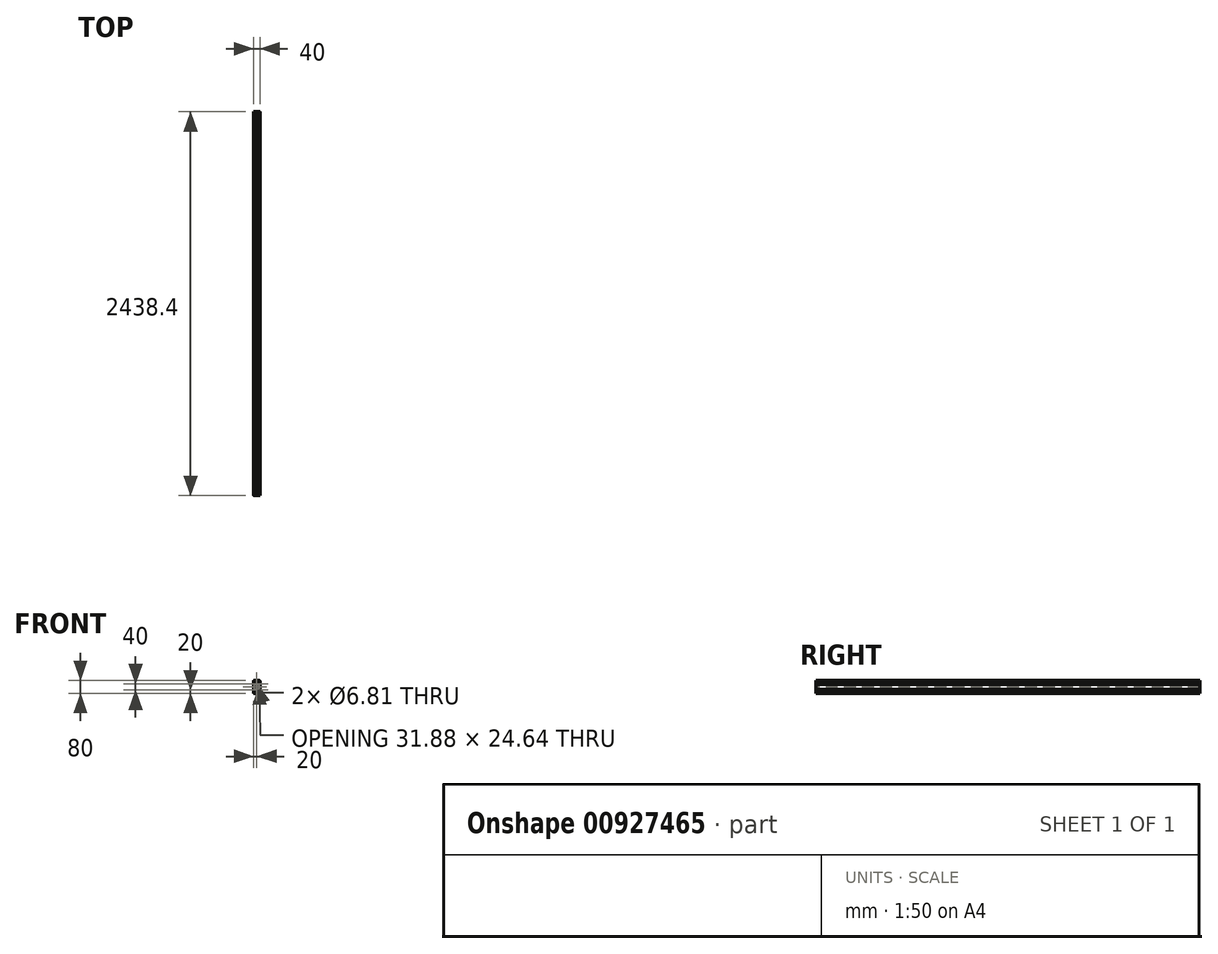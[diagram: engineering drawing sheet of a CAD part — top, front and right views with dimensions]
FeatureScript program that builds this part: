
annotation { "Feature Type Name" : "Feature", "Feature Type Description" : "" }
export const myFeature = defineFeature(function(context is Context, id is Id, definition is map)
    precondition{}
    {
        {
            var Q0;
            Q0=qCreatedBy(makeId("Front.planeOp"),FACE);
            var sketch = newSketch(context, id + "F0", { "sketchPlane" : qUnion([Q0])});
            skLineSegment(sketch, "E0.top", {"start": v(18.35, 40) * mm, "end": v(4.06, 40) * mm});
            skPoint(sketch, "E0.middle", {"position": v(0, 0) * mm});
            skArc(sketch, "E1", {"start": v(0, 16.6) * mm, "mid": v(3.4, 20) * mm, "end": v(0, 23.4) * mm});
            skLineSegment(sketch, "E2.bottom", {"start": v(20, 24.07) * mm, "end": v(15.94, 24.07) * mm});
            skLineSegment(sketch, "E2.top", {"start": v(20, 15.94) * mm, "end": v(15.94, 15.94) * mm});
            skLineSegment(sketch, "E3.top", {"start": v(15.94, 9.72) * mm, "end": v(12.62, 9.72) * mm});
            skLineSegment(sketch, "E4.right", {"start": v(15.94, 30.29) * mm, "end": v(15.94, 24.07) * mm});
            skLineSegment(sketch, "E5.MirrorCS", {"start": v(4.06, 40) * mm, "end": v(4.06, 35.94) * mm});
            skLineSegment(sketch, "E6.MirrorCS", {"start": v(10.28, 35.94) * mm, "end": v(4.06, 35.94) * mm});
            skLineSegment(sketch, "E7.MirrorCS", {"start": v(10.28, 35.94) * mm, "end": v(10.28, 32.62) * mm});
            skLineSegment(sketch, "E8.trimOffspring", {"start": v(20, 24.07) * mm, "end": v(20, 38.35) * mm});
            skLineSegment(sketch, "E9.trimOffspring", {"start": v(15.94, 15.94) * mm, "end": v(15.94, 9.72) * mm});
            skLineSegment(sketch, "E10.bottom", {"start": v(15.94, 30.29) * mm, "end": v(12.62, 30.29) * mm});
            skLineSegment(sketch, "E11.trimOffspring", {"start": v(7.68, 25.35) * mm, "end": v(7.68, 14.65) * mm});
            skLineSegment(sketch, "E12.trimOffspring", {"start": v(5.35, 27.68) * mm, "end": v(-5.35, 27.68) * mm});
            skLineSegment(sketch, "E13.trimOffspring", {"start": v(10.28, 32.62) * mm, "end": v(5.35, 27.68) * mm});
            skLineSegment(sketch, "E14.trimOffspring", {"start": v(12.62, 30.29) * mm, "end": v(7.68, 25.35) * mm});
            skLineSegment(sketch, "E15.trimOffspring", {"start": v(5.35, 12.32) * mm, "end": v(-5.35, 12.32) * mm});
            skLineSegment(sketch, "E16", {"start": v(11.25, 6.41) * mm, "end": v(15.94, 6.41) * mm});
            skLineSegment(sketch, "E17.trimOffspring", {"start": v(11.25, 6.41) * mm, "end": v(5.35, 12.32) * mm});
            skLineSegment(sketch, "E18.trimOffspring", {"start": v(12.62, 9.72) * mm, "end": v(7.68, 14.65) * mm});
            skPoint(sketch, "E19.visualSharp", {"position": v(20, 40) * mm});
            skArc(sketch, "E19.filletArc", {"start": v(20, 38.35) * mm, "mid": v(19.52, 39.52) * mm, "end": v(18.35, 40) * mm});
            skLineSegment(sketch, "E20.MirrorCS", {"start": v(15.94, -9.71) * mm, "end": v(12.62, -9.71) * mm});
            skLineSegment(sketch, "E21.MirrorCS", {"start": v(10.28, -35.94) * mm, "end": v(10.28, -32.62) * mm});
            skLineSegment(sketch, "E22.MirrorCS", {"start": v(15.94, -9.72) * mm, "end": v(12.62, -9.72) * mm});
            skArc(sketch, "E23.MirrorCS", {"start": v(20, -38.35) * mm, "mid": v(19.52, -39.52) * mm, "end": v(18.35, -40) * mm});
            skLineSegment(sketch, "E24.MirrorCS", {"start": v(15.94, -30.29) * mm, "end": v(12.62, -30.29) * mm});
            skLineSegment(sketch, "E25.MirrorCS", {"start": v(20, -24.07) * mm, "end": v(15.94, -24.07) * mm});
            skLineSegment(sketch, "E26.MirrorCS", {"start": v(5.35, -27.68) * mm, "end": v(-5.35, -27.68) * mm});
            skArc(sketch, "E27.MirrorCS", {"start": v(0, -16.6) * mm, "mid": v(3.4, -20) * mm, "end": v(0, -23.4) * mm});
            skLineSegment(sketch, "E28.MirrorCS", {"start": v(5.35, -12.32) * mm, "end": v(-5.35, -12.32) * mm});
            skLineSegment(sketch, "E29.MirrorCS", {"start": v(7.68, -25.35) * mm, "end": v(7.68, -14.65) * mm});
            skLineSegment(sketch, "E30.MirrorCS", {"start": v(10.28, -35.94) * mm, "end": v(4.06, -35.94) * mm});
            skLineSegment(sketch, "E31.MirrorCS", {"start": v(15.94, -30.28) * mm, "end": v(15.94, -24.07) * mm});
            skLineSegment(sketch, "E32.MirrorCS", {"start": v(20, -24.07) * mm, "end": v(20, -38.35) * mm});
            skLineSegment(sketch, "E33.MirrorCS", {"start": v(20, -24.06) * mm, "end": v(15.94, -24.06) * mm});
            skLineSegment(sketch, "E34.MirrorCS", {"start": v(20, -15.93) * mm, "end": v(15.94, -15.93) * mm});
            skLineSegment(sketch, "E35.MirrorCS", {"start": v(18.35, -40) * mm, "end": v(4.06, -40) * mm});
            skLineSegment(sketch, "E36.MirrorCS", {"start": v(4.06, -40) * mm, "end": v(4.06, -35.94) * mm});
            skLineSegment(sketch, "E37.MirrorCS", {"start": v(11.25, -6.41) * mm, "end": v(15.94, -6.41) * mm});
            skLineSegment(sketch, "E38.MirrorCS", {"start": v(15.94, -15.93) * mm, "end": v(15.94, -9.72) * mm});
            skPoint(sketch, "E39.MirrorP", {"position": v(20, -40) * mm});
            skLineSegment(sketch, "E40.MirrorCS", {"start": v(12.62, -30.29) * mm, "end": v(7.68, -25.35) * mm});
            skLineSegment(sketch, "E41.MirrorCS", {"start": v(11.25, -6.41) * mm, "end": v(5.35, -12.32) * mm});
            skLineSegment(sketch, "E42.MirrorCS", {"start": v(12.62, -9.72) * mm, "end": v(7.68, -14.65) * mm});
            skLineSegment(sketch, "E43.MirrorCS", {"start": v(10.28, -32.62) * mm, "end": v(5.35, -27.68) * mm});
            skLineSegment(sketch, "E44", {"start": v(15.94, 6.41) * mm, "end": v(15.94, -6.41) * mm});
            skLineSegment(sketch, "E45", {"start": v(20, 15.94) * mm, "end": v(20, -15.93) * mm});
            skLineSegment(sketch, "E46.MirrorCS", {"start": v(-15.94, -9.71) * mm, "end": v(-12.62, -9.71) * mm});
            skLineSegment(sketch, "E47.MirrorCS", {"start": v(-20, 24.07) * mm, "end": v(-15.94, 24.07) * mm});
            skLineSegment(sketch, "E48.MirrorCS", {"start": v(-15.94, 9.72) * mm, "end": v(-12.62, 9.72) * mm});
            skLineSegment(sketch, "E49.MirrorCS", {"start": v(-10.28, 35.94) * mm, "end": v(-10.28, 32.62) * mm});
            skLineSegment(sketch, "E50.MirrorCS", {"start": v(-10.28, -35.94) * mm, "end": v(-10.28, -32.62) * mm});
            skLineSegment(sketch, "E51.MirrorCS", {"start": v(-20, -24.06) * mm, "end": v(-15.94, -24.06) * mm});
            skLineSegment(sketch, "E52.MirrorCS", {"start": v(-20, -24.07) * mm, "end": v(-15.94, -24.07) * mm});
            skLineSegment(sketch, "E53.MirrorCS", {"start": v(-15.94, -9.72) * mm, "end": v(-12.62, -9.72) * mm});
            skArc(sketch, "E54.MirrorCS", {"start": v(-20, 38.35) * mm, "mid": v(-19.52, 39.52) * mm, "end": v(-18.35, 40) * mm});
            skLineSegment(sketch, "E55.MirrorCS", {"start": v(-4.06, 40) * mm, "end": v(-4.06, 35.94) * mm});
            skLineSegment(sketch, "E56.MirrorCS", {"start": v(-10.28, -32.62) * mm, "end": v(-5.35, -27.68) * mm});
            skLineSegment(sketch, "E57.MirrorCS", {"start": v(-11.25, 6.41) * mm, "end": v(-15.94, 6.41) * mm});
            skLineSegment(sketch, "E58.MirrorCS", {"start": v(-11.25, -6.41) * mm, "end": v(-15.94, -6.41) * mm});
            skLineSegment(sketch, "E59.MirrorCS", {"start": v(-4.06, -40) * mm, "end": v(-4.06, -35.94) * mm});
            skArc(sketch, "E60.MirrorCS", {"start": v(-20, -38.35) * mm, "mid": v(-19.52, -39.52) * mm, "end": v(-18.35, -40) * mm});
            skLineSegment(sketch, "E61.MirrorCS", {"start": v(-20, -15.93) * mm, "end": v(-15.94, -15.93) * mm});
            skLineSegment(sketch, "E62.MirrorCS", {"start": v(-15.94, 30.29) * mm, "end": v(-12.62, 30.29) * mm});
            skLineSegment(sketch, "E63.MirrorCS", {"start": v(-20, 15.94) * mm, "end": v(-15.94, 15.94) * mm});
            skLineSegment(sketch, "E64.MirrorCS", {"start": v(-15.94, -30.29) * mm, "end": v(-12.62, -30.29) * mm});
            skLineSegment(sketch, "E65.MirrorCS", {"start": v(-10.28, 32.62) * mm, "end": v(-5.35, 27.68) * mm});
            skPoint(sketch, "E66.MirrorP", {"position": v(-20, -40) * mm});
            skLineSegment(sketch, "E67.MirrorCS", {"start": v(-10.28, 35.94) * mm, "end": v(-4.06, 35.94) * mm});
            skLineSegment(sketch, "E68.MirrorCS", {"start": v(-18.35, 40) * mm, "end": v(-4.06, 40) * mm});
            skLineSegment(sketch, "E69.MirrorCS", {"start": v(-15.94, 15.94) * mm, "end": v(-15.94, 9.72) * mm});
            skLineSegment(sketch, "E70.MirrorCS", {"start": v(-20, -24.07) * mm, "end": v(-20, -38.35) * mm});
            skLineSegment(sketch, "E71.MirrorCS", {"start": v(-10.28, -35.94) * mm, "end": v(-4.06, -35.94) * mm});
            skLineSegment(sketch, "E72.MirrorCS", {"start": v(-15.94, -15.93) * mm, "end": v(-15.94, -9.72) * mm});
            skLineSegment(sketch, "E73.MirrorCS", {"start": v(-11.25, -6.41) * mm, "end": v(-5.35, -12.32) * mm});
            skLineSegment(sketch, "E74.MirrorCS", {"start": v(-7.68, 25.35) * mm, "end": v(-7.68, 14.65) * mm});
            skLineSegment(sketch, "E75.MirrorCS", {"start": v(-15.94, -30.28) * mm, "end": v(-15.94, -24.07) * mm});
            skLineSegment(sketch, "E76.MirrorCS", {"start": v(-15.94, 30.29) * mm, "end": v(-15.94, 24.07) * mm});
            skLineSegment(sketch, "E77.MirrorCS", {"start": v(-20, 24.07) * mm, "end": v(-20, 38.35) * mm});
            skLineSegment(sketch, "E78.MirrorCS", {"start": v(-7.68, -25.35) * mm, "end": v(-7.68, -14.65) * mm});
            skArc(sketch, "E79.MirrorCS", {"start": v(0, 16.6) * mm, "mid": v(-3.4, 20) * mm, "end": v(0, 23.4) * mm});
            skPoint(sketch, "E80.MirrorP", {"position": v(-20, 40) * mm});
            skArc(sketch, "E81.MirrorCS", {"start": v(0, -16.6) * mm, "mid": v(-3.4, -20) * mm, "end": v(0, -23.4) * mm});
            skLineSegment(sketch, "E82.MirrorCS", {"start": v(-12.62, -30.29) * mm, "end": v(-7.68, -25.35) * mm});
            skLineSegment(sketch, "E83.MirrorCS", {"start": v(-20, 15.94) * mm, "end": v(-20, -15.93) * mm});
            skLineSegment(sketch, "E84.MirrorCS", {"start": v(-12.62, 30.29) * mm, "end": v(-7.68, 25.35) * mm});
            skLineSegment(sketch, "E85.MirrorCS", {"start": v(-12.62, -9.72) * mm, "end": v(-7.68, -14.65) * mm});
            skLineSegment(sketch, "E86.MirrorCS", {"start": v(-15.94, 6.41) * mm, "end": v(-15.94, -6.41) * mm});
            skLineSegment(sketch, "E87.MirrorCS", {"start": v(-11.25, 6.41) * mm, "end": v(-5.35, 12.32) * mm});
            skLineSegment(sketch, "E88.MirrorCS", {"start": v(-12.62, 9.72) * mm, "end": v(-7.68, 14.65) * mm});
            skLineSegment(sketch, "E89.MirrorCS", {"start": v(-18.35, -40) * mm, "end": v(-4.06, -40) * mm});
            skSolve(sketch);
        }
        {
            var Q0;
            Q0=makeQuery(id+"F0.imprint","IMPRINT",FACE,{"disambiguationData":[TD([[makeQuery(id+"F0.imprint","IMPRINT",EDGE,{"derivedFrom":sQuery(id+"F0.wireOp",EDGE,"E0.top")}),1.0]])]});
            extrude(context, id + "F1", {"entities" : qUnion([Q0]), "oppositeDirection" : true, "depth" : 2438.4 * mm, "offsetDistance" : 25 * mm});
        }
    });
